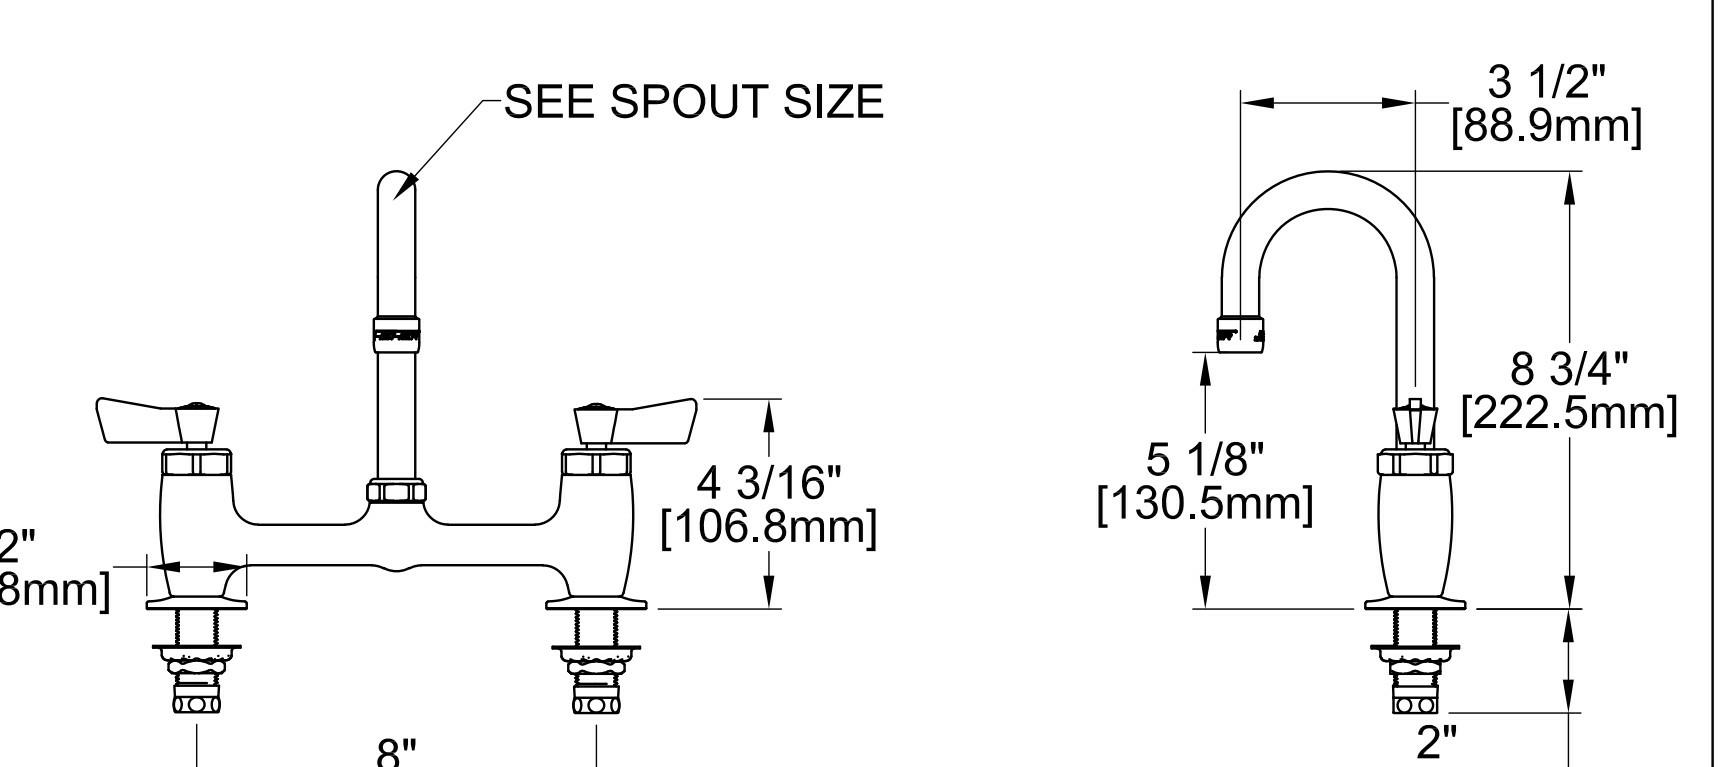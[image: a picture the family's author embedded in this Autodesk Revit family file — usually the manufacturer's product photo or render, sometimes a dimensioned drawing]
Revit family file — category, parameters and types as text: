
# Revit family: FACB-BR-4BSLL_19960
name_source: partatom
category: Plumbing Fixtures
units: mm (PartAtom-declared; Revit-internal decimal feet)

## family parameters
Always vertical = Yes
Cut with Voids When Loaded = No
OmniClass Number = 23.45.00.00
OmniClass Title = Sanitary, Laundry, and Cleaning Equipment
Part Type = Normal
Room Calculation Point = No
Round Connector Dimension = Use Diameter
Shared = No
Work Plane-Based = No

## types (1)
- FACB-BR-4BSLL_19960
    Cold Water Consumption = 0 GPM
    Cold Water Flow = 2 GPM
    Cold Water Maximum Pressure = 200.00 psi
    Cold Water Minimum Pressure = 80.00 psi
    Cold Water Size = 1/2"
    Cold Water Temperature Recommended = 40 °F
    Fixture Height = 4' - 0"
    Hot Water Consumption = 0 GPM
    Hot Water Flow = 2 GPM
    Hot Water Maximum Pressure = 200.00 psi
    Hot Water Minimum Pressure = 80.00 psi
    Hot Water Size = 1/2"
    Hot Water Temperature = 40 °F

## geometry (parser evidence)
native form markers: Sweep x10
no freeform markers — native parametric forms only
